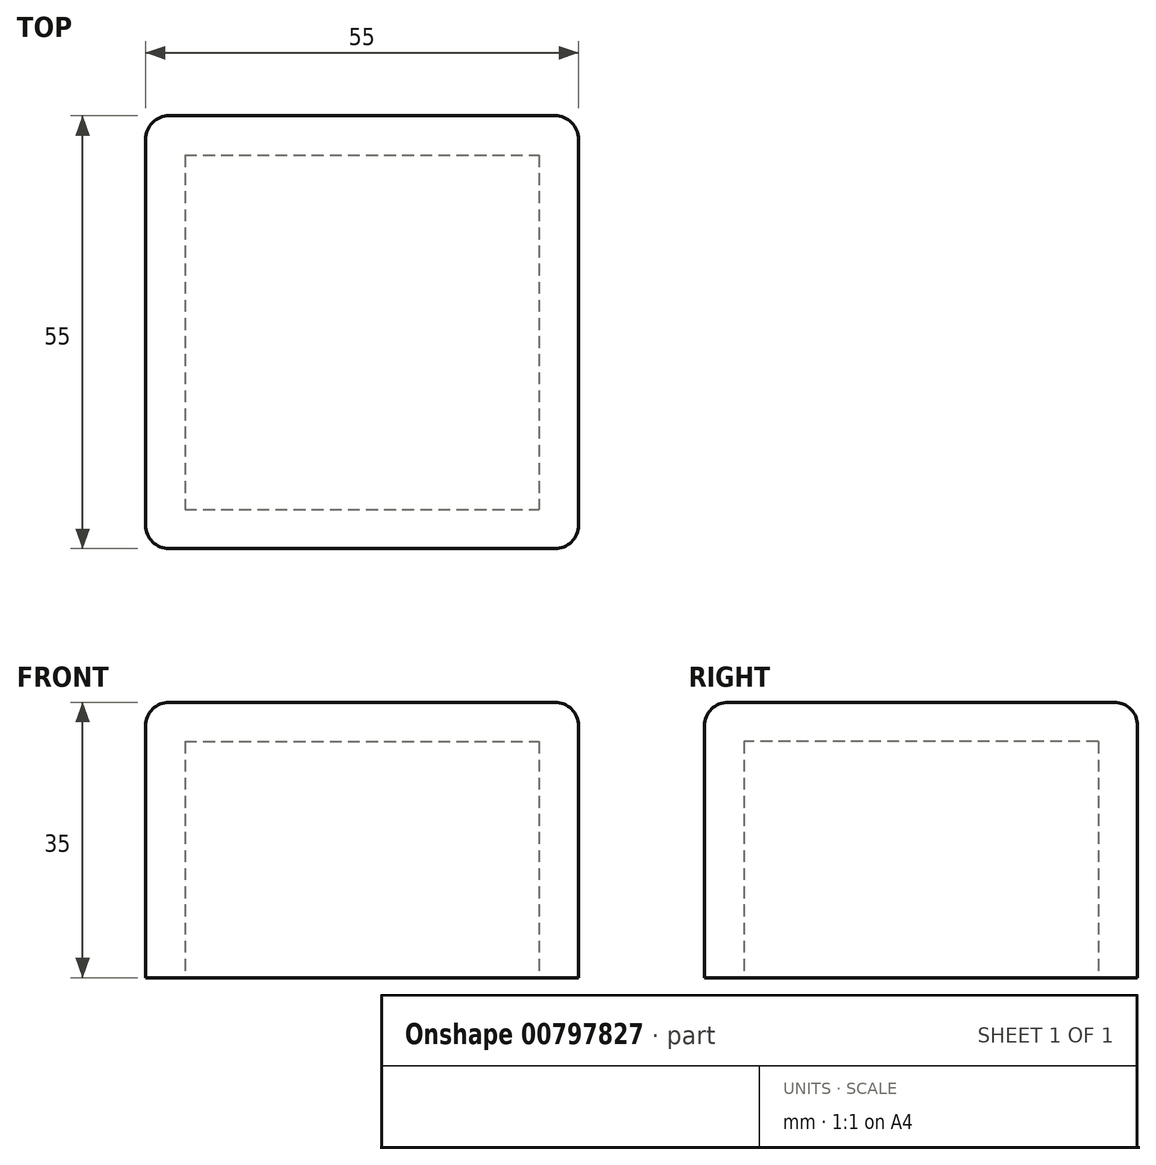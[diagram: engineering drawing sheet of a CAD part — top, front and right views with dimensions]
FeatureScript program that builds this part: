
annotation { "Feature Type Name" : "Feature", "Feature Type Description" : "" }
export const myFeature = defineFeature(function(context is Context, id is Id, definition is map)
    precondition{}
    {
        {
            var Q0;
            Q0=qCreatedBy(makeId("Top.planeOp"),FACE);
            var sketch = newSketch(context, id + "F0", { "sketchPlane" : qUnion([Q0])});
            skLineSegment(sketch, "E0.bottom", {"start": v(-62.76, 58.84) * mm, "end": v(-7.76, 58.84) * mm});
            skLineSegment(sketch, "E0.top", {"start": v(-62.76, 3.84) * mm, "end": v(-7.76, 3.84) * mm});
            skLineSegment(sketch, "E0.left", {"start": v(-62.76, 58.84) * mm, "end": v(-62.76, 3.84) * mm});
            skLineSegment(sketch, "E0.right", {"start": v(-7.76, 58.84) * mm, "end": v(-7.76, 3.84) * mm});
            skSolve(sketch);
        }
        {
            var Q0;
            Q0=makeQuery(id+"F0.imprint","IMPRINT",FACE,{"disambiguationData":[TD([[makeQuery(id+"F0.imprint","IMPRINT",EDGE,{"derivedFrom":sQuery(id+"F0.wireOp",EDGE,"E0.bottom")}),-1.0]])]});
            extrude(context, id + "F1", {"entities" : qUnion([Q0]), "depth" : 35 * mm, "offsetDistance" : 25 * mm});
        }
        {
            var Q0;
            Q0=makeQuery(id+"F1.opExtrude","CAP_FACE",FACE,{"disambiguationData":[OSD([sQuery(id+"F0.wireOp",EDGE,"E0.bottom"),sQuery(id+"F0.wireOp",EDGE,"E0.top"),sQuery(id+"F0.wireOp",EDGE,"E0.left"),sQuery(id+"F0.wireOp",EDGE,"E0.right")])],"isStart":true});
            var sketch = newSketch(context, id + "F2", { "sketchPlane" : qUnion([Q0])});
            skLineSegment(sketch, "E1.bottom", {"start": v(-57.76, -53.84) * mm, "end": v(-12.76, -53.84) * mm});
            skLineSegment(sketch, "E1.top", {"start": v(-57.76, -8.84) * mm, "end": v(-12.76, -8.84) * mm});
            skLineSegment(sketch, "E1.left", {"start": v(-57.76, -53.84) * mm, "end": v(-57.76, -8.84) * mm});
            skLineSegment(sketch, "E1.right", {"start": v(-12.76, -53.84) * mm, "end": v(-12.76, -8.84) * mm});
            skSolve(sketch);
        }
        {
            var Q0;
            Q0=makeQuery(id+"F2.imprint","IMPRINT",FACE,{"disambiguationData":[TD([[makeQuery(id+"F2.imprint","IMPRINT",EDGE,{"derivedFrom":sQuery(id+"F2.wireOp",EDGE,"E1.bottom")}),1.0]])]});
            extrude(context, id + "F3", {"entities" : qUnion([Q0]), "operationType" : NewBodyOperationType.REMOVE, "oppositeDirection" : true, "depth" : 30 * mm, "offsetDistance" : 25 * mm});
        }
        {
            var Q0;
            Q0=makeQuery(id+"F1.opExtrude","CAP_EDGE",EDGE,{"disambiguationData":[OSD([sQuery(id+"F0.wireOp",EDGE,"E0.left")])],"isStart":false});
            var Q1;
            Q1=makeQuery(id+"F1.opExtrude","CAP_EDGE",EDGE,{"disambiguationData":[OSD([sQuery(id+"F0.wireOp",EDGE,"E0.top")])],"isStart":false});
            var Q2;
            Q2=makeQuery(id+"F1.opExtrude","SWEPT_EDGE",EDGE,{"disambiguationData":[OSD([sQuery(id+"F0.wireOp",EDGE,"E0.top"),sQuery(id+"F0.wireOp",EDGE,"E0.left")])]});
            var Q3;
            Q3=makeQuery(id+"F1.opExtrude","CAP_EDGE",EDGE,{"disambiguationData":[OSD([sQuery(id+"F0.wireOp",EDGE,"E0.right")])],"isStart":false});
            var Q4;
            Q4=makeQuery(id+"F1.opExtrude","CAP_EDGE",EDGE,{"disambiguationData":[OSD([sQuery(id+"F0.wireOp",EDGE,"E0.bottom")])],"isStart":false});
            var Q5;
            Q5=makeQuery(id+"F1.opExtrude","SWEPT_EDGE",EDGE,{"disambiguationData":[OSD([sQuery(id+"F0.wireOp",EDGE,"E0.bottom"),sQuery(id+"F0.wireOp",EDGE,"E0.left")])]});
            var Q6;
            Q6=makeQuery(id+"F1.opExtrude","SWEPT_EDGE",EDGE,{"disambiguationData":[OSD([sQuery(id+"F0.wireOp",EDGE,"E0.bottom"),sQuery(id+"F0.wireOp",EDGE,"E0.right")])]});
            var Q7;
            Q7=makeQuery(id+"F1.opExtrude","SWEPT_EDGE",EDGE,{"disambiguationData":[OSD([sQuery(id+"F0.wireOp",EDGE,"E0.top"),sQuery(id+"F0.wireOp",EDGE,"E0.right")])]});
            fillet(context, id + "F4", {"entities" : qUnion([Q0, Q1, Q2, Q3, Q4, Q5, Q6, Q7]), "radius" : 3 * mm, "tangentPropagation" : true, "allowEdgeOverflow" : false});
        }
    });
